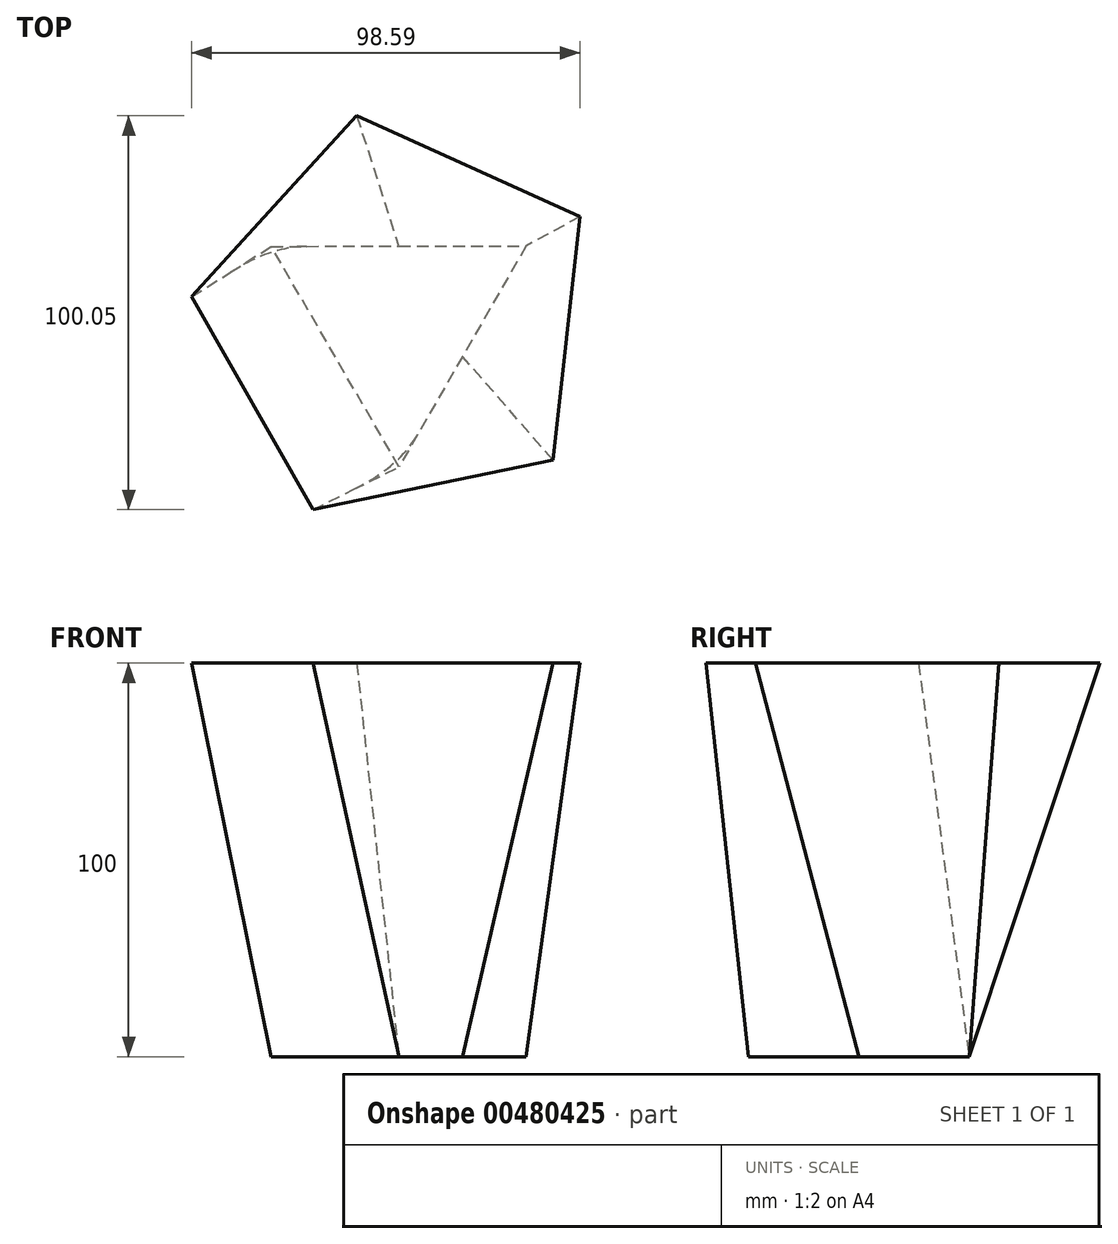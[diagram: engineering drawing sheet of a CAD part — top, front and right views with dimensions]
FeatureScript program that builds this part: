
annotation { "Feature Type Name" : "Feature", "Feature Type Description" : "" }
export const myFeature = defineFeature(function(context is Context, id is Id, definition is map)
    precondition{}
    {
        {
            var Q0;
            Q0=qCreatedBy(makeId("Top.planeOp"),FACE);
            var sketch = newSketch(context, id + "F0", { "sketchPlane" : qUnion([Q0])});
            skCircle(sketch, "E0.cCircle", {"center": v(0, 0) * mm, "radius": 37.38 * mm, "construction": true});
            skLineSegment(sketch, "E0.0", {"start": v(32.35, 18.74) * mm, "end": v(0.06, -37.38) * mm});
            skLineSegment(sketch, "E0.1", {"start": v(0.06, -37.38) * mm, "end": v(-32.4, 18.64) * mm});
            skLineSegment(sketch, "E0.2", {"start": v(-32.4, 18.64) * mm, "end": v(32.35, 18.74) * mm});
            skSolve(sketch);
        }
        {
            var Q0;
            Q0=qCreatedBy(makeId("Top.planeOp"),FACE);
            cPlane(context, id + "F1", {"entities" : qUnion([Q0]), "cplaneType" : CPlaneType.OFFSET, "offset" : 100 * mm, "width" : 152.4 * mm, "height" : 152.4 * mm});
        }
        {
            var Q0;
            Q0=qCreatedBy(id+"F1.planeOp",FACE);
            var sketch = newSketch(context, id + "F2", { "sketchPlane" : qUnion([Q0])});
            skCircle(sketch, "E1.cCircle", {"center": v(0, 0) * mm, "radius": 52.92 * mm, "construction": true});
            skLineSegment(sketch, "E1.0", {"start": v(45.99, 26.2) * mm, "end": v(39.12, -35.64) * mm});
            skLineSegment(sketch, "E1.1", {"start": v(39.12, -35.64) * mm, "end": v(-21.8, -48.22) * mm});
            skLineSegment(sketch, "E1.2", {"start": v(-21.8, -48.22) * mm, "end": v(-52.6, 5.84) * mm});
            skLineSegment(sketch, "E1.3", {"start": v(-52.6, 5.84) * mm, "end": v(-10.7, 51.83) * mm});
            skLineSegment(sketch, "E1.4", {"start": v(-10.7, 51.83) * mm, "end": v(45.99, 26.2) * mm});
            skSolve(sketch);
        }
        {
            var Q0;
            Q0=makeQuery(id+"F2.imprint","IMPRINT",FACE,{"disambiguationData":[TD([[makeQuery(id+"F2.imprint","IMPRINT",EDGE,{"derivedFrom":sQuery(id+"F2.wireOp",EDGE,"E1.0")}),-1.0]])]});
            var Q1;
            Q1=makeQuery(id+"F0.imprint","IMPRINT",FACE,{"disambiguationData":[TD([[makeQuery(id+"F0.imprint","IMPRINT",EDGE,{"derivedFrom":sQuery(id+"F0.wireOp",EDGE,"E0.0")}),-1.0]])]});
            loft(context, id + "F3", {"sheetProfilesArray" : [{ "sheetProfileEntities" : qUnion([Q0]) }, { "sheetProfileEntities" : qUnion([Q1]) }]});
        }
    });
